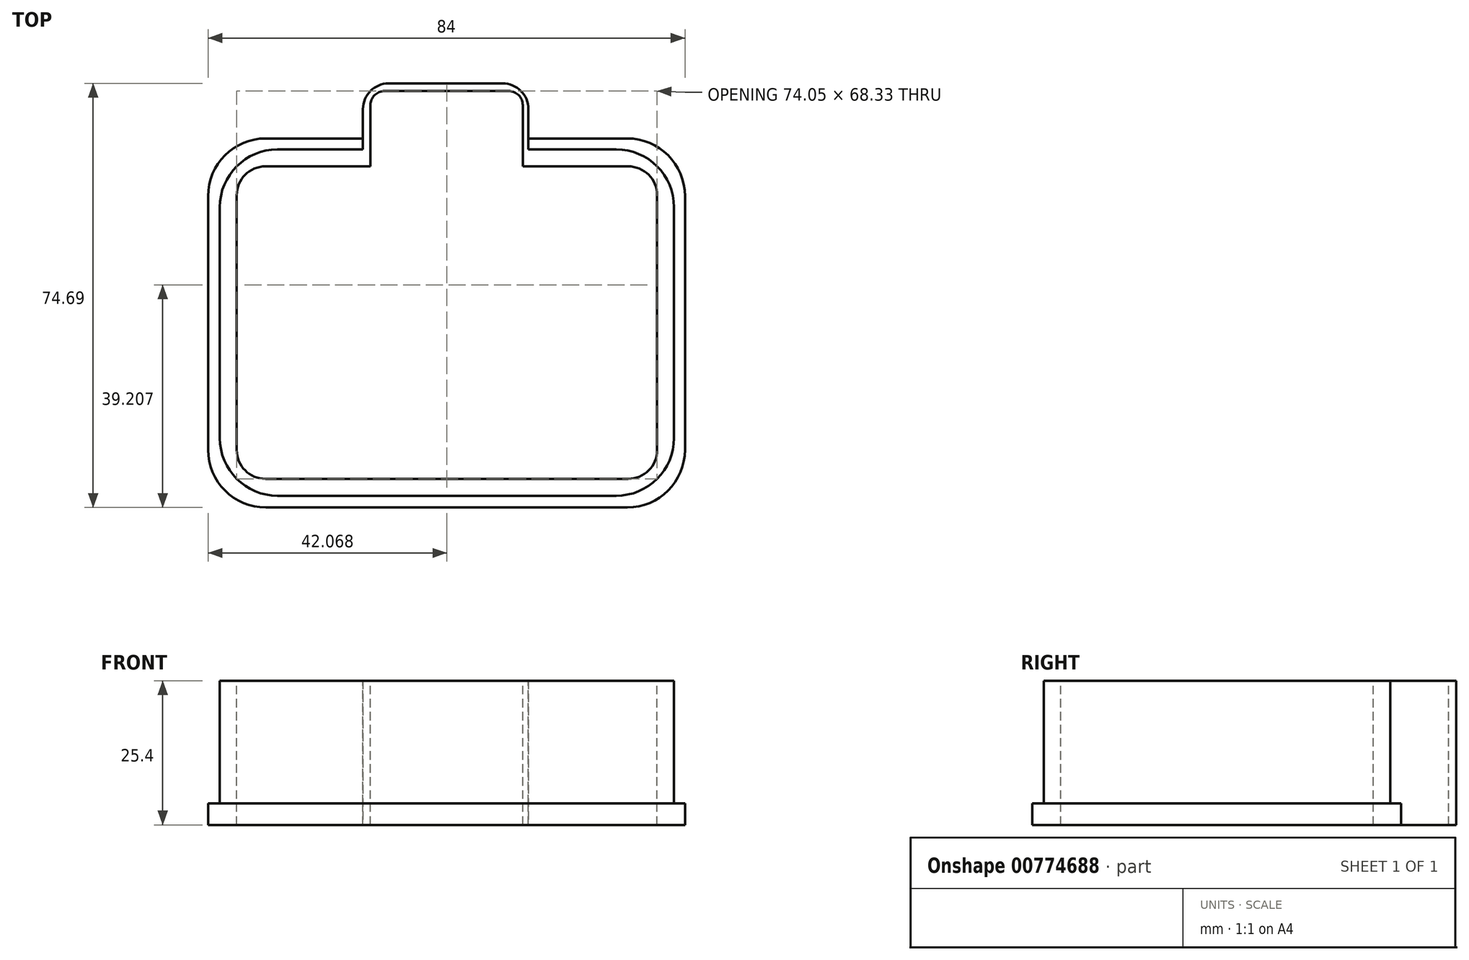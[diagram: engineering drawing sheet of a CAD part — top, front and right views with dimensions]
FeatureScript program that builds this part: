
annotation { "Feature Type Name" : "Feature", "Feature Type Description" : "" }
export const myFeature = defineFeature(function(context is Context, id is Id, definition is map)
    precondition{}
    {
        {
            var Q0;
            Q0=qCreatedBy(makeId("Top.planeOp"),FACE);
            var sketch = newSketch(context, id + "F0", { "sketchPlane" : qUnion([Q0])});
            skLineSegment(sketch, "E0.bottom", {"start": v(-33.95, 31.7) * mm, "end": v(29.73, 31.7) * mm});
            skLineSegment(sketch, "E0.top", {"start": v(-33.95, -33.3) * mm, "end": v(29.73, -33.3) * mm});
            skLineSegment(sketch, "E0.left", {"start": v(-44.1, 21.54) * mm, "end": v(-44.1, -23.14) * mm});
            skLineSegment(sketch, "E0.right", {"start": v(39.9, 21.54) * mm, "end": v(39.9, -23.14) * mm});
            skPoint(sketch, "E1.visualSharp", {"position": v(-44.1, 31.7) * mm});
            skArc(sketch, "E1.filletArc", {"start": v(-33.95, 31.7) * mm, "mid": v(-41.13, 28.73) * mm, "end": v(-44.1, 21.54) * mm});
            skPoint(sketch, "E2.visualSharp", {"position": v(39.9, 31.7) * mm});
            skArc(sketch, "E2.filletArc", {"start": v(39.9, 21.54) * mm, "mid": v(36.92, 28.73) * mm, "end": v(29.73, 31.7) * mm});
            skPoint(sketch, "E3.visualSharp", {"position": v(39.9, -33.3) * mm});
            skArc(sketch, "E3.filletArc", {"start": v(29.73, -33.3) * mm, "mid": v(36.92, -30.32) * mm, "end": v(39.9, -23.14) * mm});
            skPoint(sketch, "E4.visualSharp", {"position": v(-44.1, -33.3) * mm});
            skArc(sketch, "E4.filletArc", {"start": v(-44.1, -23.14) * mm, "mid": v(-41.13, -30.32) * mm, "end": v(-33.95, -33.3) * mm});
            skSolve(sketch);
        }
        {
            var Q0;
            Q0=qCreatedBy(makeId("Top.planeOp"),FACE);
            var sketch = newSketch(context, id + "F1", { "sketchPlane" : qUnion([Q0])});
            skLineSegment(sketch, "E5.bottom", {"start": v(-31.88, 29.77) * mm, "end": v(27.8, 29.77) * mm});
            skLineSegment(sketch, "E5.top", {"start": v(-31.88, -31.23) * mm, "end": v(27.8, -31.23) * mm});
            skLineSegment(sketch, "E5.left", {"start": v(-42.04, 19.6) * mm, "end": v(-42.04, -21.07) * mm});
            skLineSegment(sketch, "E5.right", {"start": v(37.96, 19.6) * mm, "end": v(37.96, -21.07) * mm});
            skPoint(sketch, "E6.visualSharp", {"position": v(-42.04, 29.77) * mm});
            skArc(sketch, "E6.filletArc", {"start": v(-31.88, 29.77) * mm, "mid": v(-39.07, 26.8) * mm, "end": v(-42.04, 19.6) * mm});
            skPoint(sketch, "E7.visualSharp", {"position": v(37.96, 29.77) * mm});
            skArc(sketch, "E7.filletArc", {"start": v(37.96, 19.6) * mm, "mid": v(34.98, 26.8) * mm, "end": v(27.8, 29.77) * mm});
            skPoint(sketch, "E8.visualSharp", {"position": v(37.96, -31.23) * mm});
            skArc(sketch, "E8.filletArc", {"start": v(27.8, -31.23) * mm, "mid": v(34.98, -28.26) * mm, "end": v(37.96, -21.07) * mm});
            skPoint(sketch, "E9.visualSharp", {"position": v(-42.04, -31.23) * mm});
            skArc(sketch, "E9.filletArc", {"start": v(-42.04, -21.07) * mm, "mid": v(-39.07, -28.26) * mm, "end": v(-31.88, -31.23) * mm});
            skSolve(sketch);
        }
        {
            var Q0;
            Q0=makeQuery(id+"F1.imprint","IMPRINT",FACE,{"disambiguationData":[TD([[makeQuery(id+"F1.imprint","IMPRINT",EDGE,{"derivedFrom":sQuery(id+"F1.wireOp",EDGE,"E5.bottom")}),-1.0]])]});
            extrude(context, id + "F2", {"entities" : qUnion([Q0]), "depth" : 25.4 * mm, "offsetDistance" : 25.4 * mm});
        }
        {
            var Q0;
            Q0=makeQuery(id+"F2.opExtrude","CAP_FACE",FACE,{"disambiguationData":[OSD([sQuery(id+"F1.wireOp",EDGE,"E5.bottom"),sQuery(id+"F1.wireOp",EDGE,"E5.top"),sQuery(id+"F1.wireOp",EDGE,"E5.left"),sQuery(id+"F1.wireOp",EDGE,"E5.right"),sQuery(id+"F1.wireOp",EDGE,"E6.filletArc"),sQuery(id+"F1.wireOp",EDGE,"E7.filletArc"),sQuery(id+"F1.wireOp",EDGE,"E8.filletArc"),sQuery(id+"F1.wireOp",EDGE,"E9.filletArc")])],"isStart":false});
            var sketch = newSketch(context, id + "F3", { "sketchPlane" : qUnion([Q0])});
            skLineSegment(sketch, "E10.bottom", {"start": v(-33.99, 26.8) * mm, "end": v(29.9, 26.8) * mm});
            skLineSegment(sketch, "E10.top", {"start": v(-33.99, -28.26) * mm, "end": v(29.9, -28.26) * mm});
            skLineSegment(sketch, "E10.left", {"start": v(-39.07, 21.71) * mm, "end": v(-39.07, -23.18) * mm});
            skLineSegment(sketch, "E10.right", {"start": v(34.98, 21.71) * mm, "end": v(34.98, -23.18) * mm});
            skPoint(sketch, "E11.visualSharp", {"position": v(-39.07, 26.8) * mm});
            skArc(sketch, "E11.filletArc", {"start": v(-33.99, 26.8) * mm, "mid": v(-37.58, 25.3) * mm, "end": v(-39.07, 21.71) * mm});
            skPoint(sketch, "E12.visualSharp", {"position": v(34.98, 26.8) * mm});
            skArc(sketch, "E12.filletArc", {"start": v(34.98, 21.71) * mm, "mid": v(33.5, 25.3) * mm, "end": v(29.9, 26.8) * mm});
            skPoint(sketch, "E13.visualSharp", {"position": v(34.98, -28.26) * mm});
            skArc(sketch, "E13.filletArc", {"start": v(29.9, -28.26) * mm, "mid": v(33.5, -26.77) * mm, "end": v(34.98, -23.18) * mm});
            skPoint(sketch, "E14.visualSharp", {"position": v(-39.07, -28.26) * mm});
            skArc(sketch, "E14.filletArc", {"start": v(-39.07, -23.18) * mm, "mid": v(-37.58, -26.77) * mm, "end": v(-33.99, -28.26) * mm});
            skSolve(sketch);
        }
        {
            var Q0;
            Q0=makeQuery(id+"F3.imprint","IMPRINT",FACE,{"disambiguationData":[TD([[makeQuery(id+"F3.imprint","IMPRINT",EDGE,{"derivedFrom":sQuery(id+"F3.wireOp",EDGE,"E10.bottom")}),-1.0]])]});
            extrude(context, id + "F4", {"entities" : qUnion([Q0]), "operationType" : NewBodyOperationType.REMOVE, "oppositeDirection" : true, "depth" : 25.4 * mm, "offsetDistance" : 25.4 * mm});
        }
        {
            var Q0;
            Q0 = qSketchRegion(id + "F0", true);
            extrude(context, id + "F5", {"entities" : qUnion([Q0]), "operationType" : NewBodyOperationType.ADD, "depth" : 3.8 * mm, "offsetDistance" : 25.4 * mm});
        }
        {
            var Q0;
            Q0=makeQuery(id+"F5.boolean.opBoolean","SPLIT",FACE,{"disambiguationData":[TD([makeQuery(id+"F4.boolean.opBoolean","COPY",FACE,{"derivedFrom":makeQuery(id+"F4.opExtrude","SWEPT_FACE",FACE,{"disambiguationData":[OSD([sQuery(id+"F3.wireOp",EDGE,"E10.bottom")])]})})])],"derivedFrom":makeQuery(id+"F5.opExtrude","CAP_FACE",FACE,{"disambiguationData":[OSD([sQuery(id+"F0.wireOp",EDGE,"E0.bottom"),sQuery(id+"F0.wireOp",EDGE,"E0.top"),sQuery(id+"F0.wireOp",EDGE,"E0.left"),sQuery(id+"F0.wireOp",EDGE,"E0.right"),sQuery(id+"F0.wireOp",EDGE,"E1.filletArc"),sQuery(id+"F0.wireOp",EDGE,"E2.filletArc"),sQuery(id+"F0.wireOp",EDGE,"E3.filletArc"),sQuery(id+"F0.wireOp",EDGE,"E4.filletArc")])],"isStart":false})});
            extrude(context, id + "F6", {"entities" : qUnion([Q0]), "operationType" : NewBodyOperationType.REMOVE, "oppositeDirection" : true, "depth" : 25.4 * mm, "offsetDistance" : 25.4 * mm});
        }
        {
            var Q0;
            Q0=qCreatedBy(makeId("Top.planeOp"),FACE);
            var sketch = newSketch(context, id + "F7", { "sketchPlane" : qUnion([Q0])});
            skLineSegment(sketch, "E15.bottom", {"start": v(-16.83, 26.8) * mm, "end": v(12.3, 26.8) * mm});
            skLineSegment(sketch, "E15.top", {"start": v(-12.31, 41.4) * mm, "end": v(7.8, 41.4) * mm});
            skLineSegment(sketch, "E15.left", {"start": v(-16.83, 26.8) * mm, "end": v(-16.83, 36.88) * mm});
            skLineSegment(sketch, "E15.right", {"start": v(12.3, 26.8) * mm, "end": v(12.3, 36.88) * mm});
            skPoint(sketch, "E16.visualSharp", {"position": v(-16.83, 41.4) * mm});
            skArc(sketch, "E16.filletArc", {"start": v(-12.31, 41.4) * mm, "mid": v(-15.5, 40.07) * mm, "end": v(-16.83, 36.88) * mm});
            skPoint(sketch, "E17.visualSharp", {"position": v(12.3, 41.4) * mm});
            skArc(sketch, "E17.filletArc", {"start": v(12.3, 36.88) * mm, "mid": v(10.98, 40.07) * mm, "end": v(7.8, 41.4) * mm});
            skSolve(sketch);
        }
        {
            var Q0;
            Q0=makeQuery(id+"F7.imprint","IMPRINT",FACE,{"disambiguationData":[TD([[makeQuery(id+"F7.imprint","IMPRINT",EDGE,{"derivedFrom":sQuery(id+"F7.wireOp",EDGE,"E15.bottom")}),1.0]])]});
            extrude(context, id + "F8", {"entities" : qUnion([Q0]), "operationType" : NewBodyOperationType.ADD, "depth" : 25.4 * mm, "offsetDistance" : 25.4 * mm});
        }
        {
            var Q0;
            Q0=makeQuery(id+"F8.boolean.opBoolean","MERGE",FACE,{"derivedFrom":[makeQuery(id+"F2.opExtrude","CAP_FACE",FACE,{"disambiguationData":[OSD([sQuery(id+"F1.wireOp",EDGE,"E5.bottom"),sQuery(id+"F1.wireOp",EDGE,"E5.top"),sQuery(id+"F1.wireOp",EDGE,"E5.left"),sQuery(id+"F1.wireOp",EDGE,"E5.right"),sQuery(id+"F1.wireOp",EDGE,"E6.filletArc"),sQuery(id+"F1.wireOp",EDGE,"E7.filletArc"),sQuery(id+"F1.wireOp",EDGE,"E8.filletArc"),sQuery(id+"F1.wireOp",EDGE,"E9.filletArc")])],"isStart":false}),makeQuery(id+"F8.opExtrude","CAP_FACE",FACE,{"disambiguationData":[OSD([sQuery(id+"F7.wireOp",EDGE,"E15.bottom"),sQuery(id+"F7.wireOp",EDGE,"E15.top"),sQuery(id+"F7.wireOp",EDGE,"E15.left"),sQuery(id+"F7.wireOp",EDGE,"E15.right"),sQuery(id+"F7.wireOp",EDGE,"E16.filletArc"),sQuery(id+"F7.wireOp",EDGE,"E17.filletArc")])],"isStart":false})]});
            var sketch = newSketch(context, id + "F9", { "sketchPlane" : qUnion([Q0])});
            skLineSegment(sketch, "E18.bottom", {"start": v(-13, 40.07) * mm, "end": v(8.8, 40.07) * mm});
            skLineSegment(sketch, "E18.top", {"start": v(-15.5, 26.8) * mm, "end": v(11.32, 26.8) * mm});
            skLineSegment(sketch, "E18.left", {"start": v(-15.5, 37.56) * mm, "end": v(-15.5, 26.8) * mm});
            skLineSegment(sketch, "E18.right", {"start": v(11.32, 37.56) * mm, "end": v(11.32, 26.8) * mm});
            skPoint(sketch, "E19.visualSharp", {"position": v(-15.5, 40.07) * mm});
            skArc(sketch, "E19.filletArc", {"start": v(-13, 40.07) * mm, "mid": v(-14.77, 39.34) * mm, "end": v(-15.5, 37.56) * mm});
            skPoint(sketch, "E20.visualSharp", {"position": v(11.32, 40.07) * mm});
            skArc(sketch, "E20.filletArc", {"start": v(11.32, 37.56) * mm, "mid": v(10.58, 39.34) * mm, "end": v(8.8, 40.07) * mm});
            skSolve(sketch);
        }
        {
            var Q0;
            Q0=makeQuery(id+"F9.imprint","IMPRINT",FACE,{"disambiguationData":[TD([[makeQuery(id+"F9.imprint","IMPRINT",EDGE,{"derivedFrom":sQuery(id+"F9.wireOp",EDGE,"E18.bottom")}),-1.0]])]});
            extrude(context, id + "F10", {"entities" : qUnion([Q0]), "operationType" : NewBodyOperationType.REMOVE, "oppositeDirection" : true, "depth" : 25.4 * mm, "offsetDistance" : 25.4 * mm});
        }
    });
